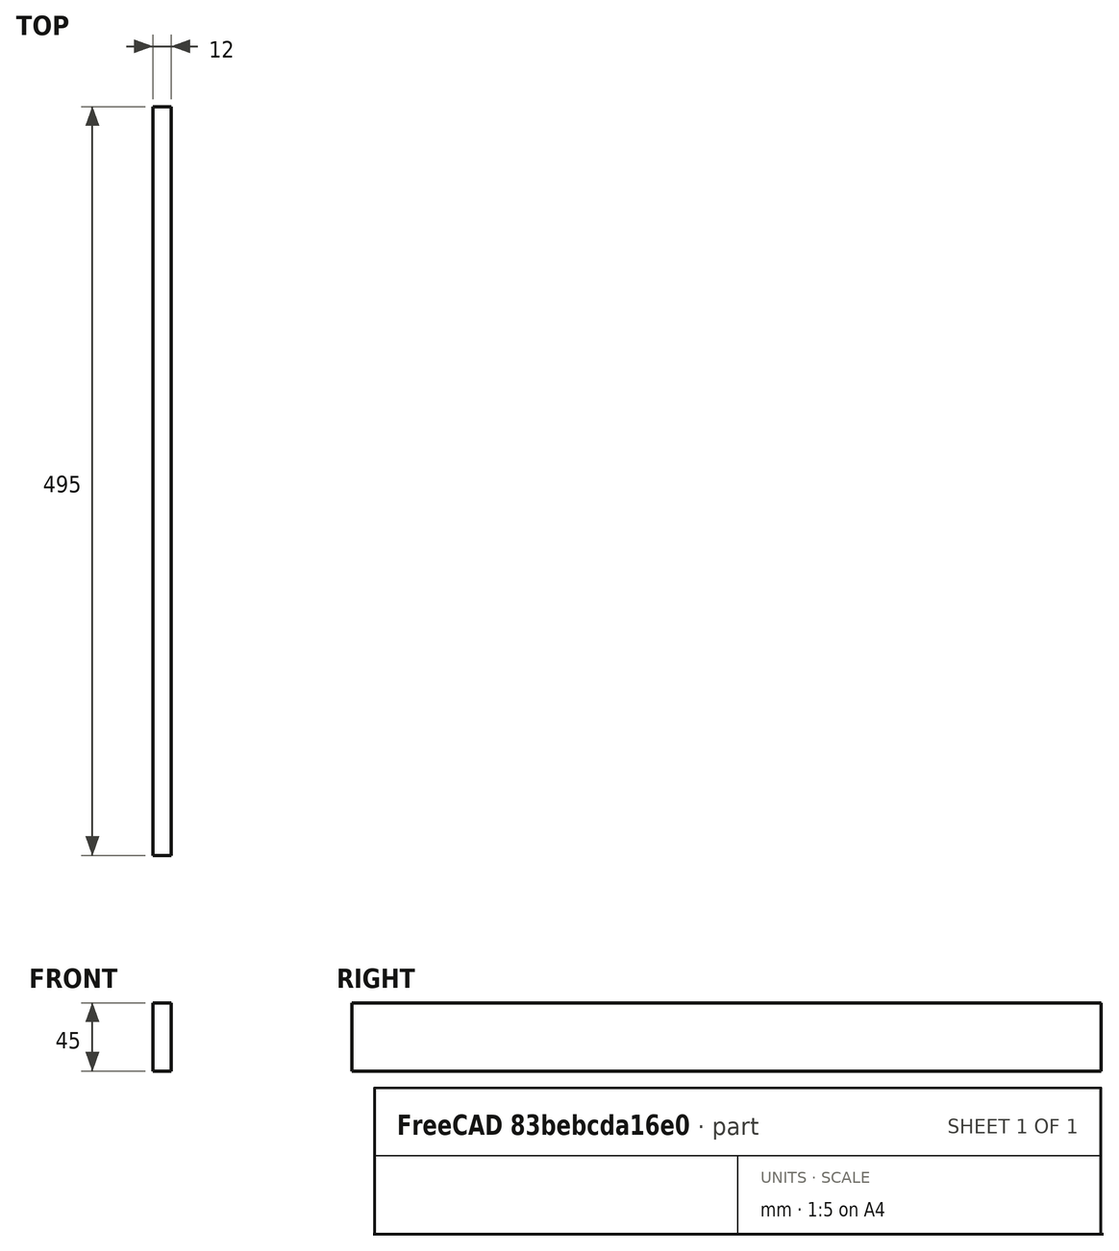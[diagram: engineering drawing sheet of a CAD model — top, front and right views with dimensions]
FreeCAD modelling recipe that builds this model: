
FCSTD DOCUMENT  (FreeCAD 0.19R24291 (Git))
Label: 8000_WindowFrameBottom_
License: All rights reserved
LicenseURL: http://en.wikipedia.org/wiki/All_rights_reserved
objects: Sketcher::SketchObject×1, Spreadsheet::Sheet×1, PartDesign::Pad×1, PartDesign::Body×1
note: 4 computed .brp shape members not serialized (recipe doc carries the construction recipe); baked Part::Feature solids carry a one-line shape summary decoded from their .brp

FEATURE [Sketcher::SketchObject] Sketch
  FullyConstrained = true
  MapMode = 4
  Placement = pos=(0,0,0) rot=(0.57735,0.57735,0.57735;2.0944rad)
  Support = -> [XY_Plane]
  expr: Constraints[6] = Spreadsheet.nY
  expr: Constraints[5] = Spreadsheet.nZ
  sketch-geometry (5):
    g0: LineSegment StartX=0 StartY=0 StartZ=0 EndX=0 EndY=45 EndZ=0
    g1: LineSegment StartX=495 StartY=0 StartZ=0 EndX=495 EndY=45 EndZ=0
    g2: LineSegment StartX=495 StartY=45 StartZ=0 EndX=0 EndY=45 EndZ=0
    g3: LineSegment StartX=247.5 StartY=0 StartZ=0 EndX=0 EndY=0 EndZ=0
    g4: LineSegment StartX=495 StartY=0 StartZ=0 EndX=247.5 EndY=0 EndZ=0
  constraints (14):
    c: Vertical(g0)
    c: Vertical(g1)
    c: Coincident(g2,g1)
    c: Coincident(g2,g0)
    c: Horizontal(g2)
    c: DistanceY(g1,g1) = 45
    c: DistanceX(g2,g2) = 495
    c: Coincident(g3,g0)
    c: Coincident(g4,g1)
    c: Horizontal(g4)
    c: Equal(g3,g4)
    c: Coincident(g4,g3)
    c: Horizontal(g3)
    c: Coincident(g0,g-1)
FEATURE [Spreadsheet::Sheet] Spreadsheet  label="xls"
  cells = B2=BODY FLOOR; E2=Ex.Ref.; B3=Thichness; C3=.T; D3=12; E3=mm; B7=KEYBOARD FRONT; D7=Sperrholz Birke 12 mm; B8=Width; C8=nY; D8(nY)=495; F8=Max Height; G8=Roof Thickness; H8=Correction; B9=Height; C9=nZ; D9(nZ)=45; E9=F(T); F9=100; G9=12; H9=2; B10=Thickness; C10=nT; D10(nT)=12
FEATURE [PartDesign::Pad] Pad
  AllowMultiFace = false
  Direction = (1,1,1)
  Length = 12
  Length2 = 100
  Profile = -> Sketch
  Reversed = true
  Type = 0
  expr: Length = Spreadsheet.nT
FEATURE [PartDesign::Body] Body
  Group = -> [Sketch,Pad]
  Origin = -> Origin
  Tip = -> Pad
